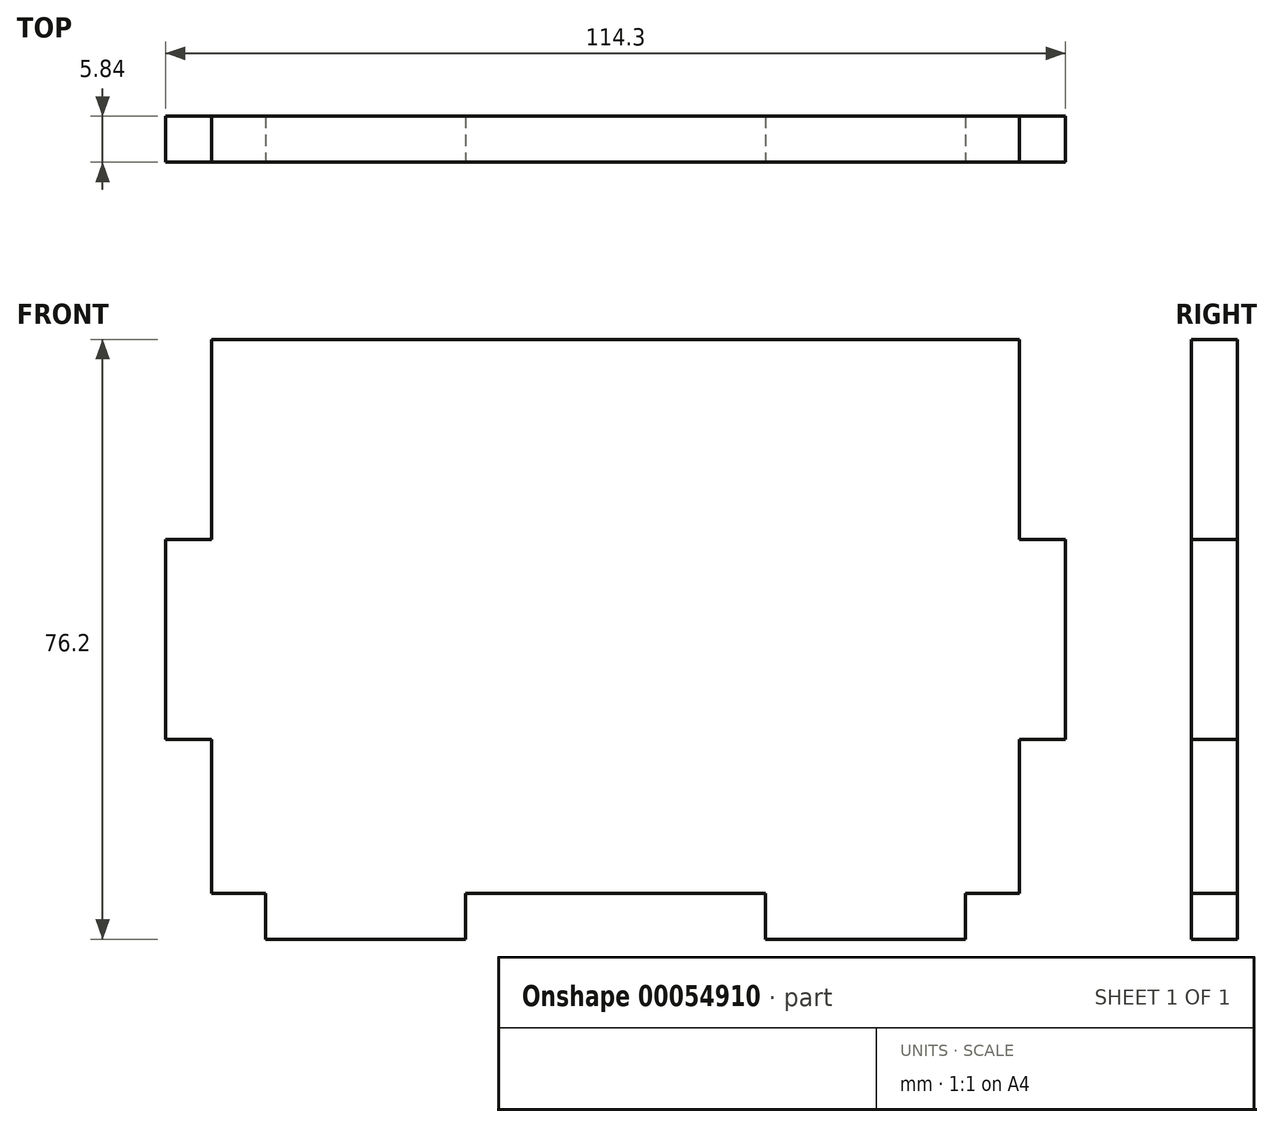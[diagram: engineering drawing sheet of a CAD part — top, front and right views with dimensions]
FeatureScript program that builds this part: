
annotation { "Feature Type Name" : "Feature", "Feature Type Description" : "" }
export const myFeature = defineFeature(function(context is Context, id is Id, definition is map)
    precondition{}
    {
        {
            var Q0;
            Q0=qCreatedBy(makeId("Front.planeOp"),FACE);
            var sketch = newSketch(context, id + "F0", { "sketchPlane" : qUnion([Q0])});
            skLineSegment(sketch, "E0.bottom", {"start": v(-48.17, 28.9) * mm, "end": v(66.13, 28.9) * mm});
            skLineSegment(sketch, "E0.top", {"start": v(-48.17, -47.3) * mm, "end": v(66.13, -47.3) * mm});
            skLineSegment(sketch, "E0.left", {"start": v(-48.17, 28.9) * mm, "end": v(-48.17, -47.3) * mm});
            skLineSegment(sketch, "E0.right", {"start": v(66.13, 28.9) * mm, "end": v(66.13, -47.3) * mm});
            skSolve(sketch);
        }
        {
            var Q0;
            Q0=makeQuery(id+"F0.imprint","IMPRINT",FACE,{"disambiguationData":[TD([[makeQuery(id+"F0.imprint","IMPRINT",EDGE,{"derivedFrom":sQuery(id+"F0.wireOp",EDGE,"E0.bottom")}),-1.0]])]});
            extrude(context, id + "F1", {"entities" : qUnion([Q0]), "depth" : 5.84 * mm});
        }
        {
            var Q0;
            Q0=makeQuery(id+"F1.opExtrude","CAP_FACE",FACE,{"disambiguationData":[OSD([sQuery(id+"F0.wireOp",EDGE,"E0.bottom"),sQuery(id+"F0.wireOp",EDGE,"E0.top"),sQuery(id+"F0.wireOp",EDGE,"E0.left"),sQuery(id+"F0.wireOp",EDGE,"E0.right")])],"isStart":false});
            var sketch = newSketch(context, id + "F2", { "sketchPlane" : qUnion([Q0])});
            skLineSegment(sketch, "E1.bottom", {"start": v(-35.47, -47.3) * mm, "end": v(-10.07, -47.3) * mm});
            skLineSegment(sketch, "E1.top", {"start": v(-35.47, -41.45) * mm, "end": v(-10.07, -41.45) * mm});
            skLineSegment(sketch, "E1.left", {"start": v(-35.47, -47.3) * mm, "end": v(-35.47, -41.45) * mm});
            skLineSegment(sketch, "E1.right", {"start": v(-10.07, -47.3) * mm, "end": v(-10.07, -41.45) * mm});
            skLineSegment(sketch, "E2.bottom", {"start": v(28.03, -47.3) * mm, "end": v(53.43, -47.3) * mm});
            skLineSegment(sketch, "E2.top", {"start": v(28.03, -41.45) * mm, "end": v(53.43, -41.45) * mm});
            skLineSegment(sketch, "E2.left", {"start": v(28.03, -47.3) * mm, "end": v(28.03, -41.45) * mm});
            skLineSegment(sketch, "E2.right", {"start": v(53.43, -47.3) * mm, "end": v(53.43, -41.45) * mm});
            skLineSegment(sketch, "E3.bottom", {"start": v(-48.17, -21.9) * mm, "end": v(-42.32, -21.9) * mm});
            skLineSegment(sketch, "E3.top", {"start": v(-48.17, 3.5) * mm, "end": v(-42.32, 3.5) * mm});
            skLineSegment(sketch, "E3.left", {"start": v(-48.17, -21.9) * mm, "end": v(-48.17, 3.5) * mm});
            skLineSegment(sketch, "E3.right", {"start": v(-42.32, -21.9) * mm, "end": v(-42.32, 3.5) * mm});
            skLineSegment(sketch, "E4.bottom", {"start": v(66.13, -21.9) * mm, "end": v(60.3, -21.9) * mm});
            skLineSegment(sketch, "E4.top", {"start": v(66.13, 3.5) * mm, "end": v(60.3, 3.5) * mm});
            skLineSegment(sketch, "E4.left", {"start": v(66.13, -21.9) * mm, "end": v(66.13, 3.5) * mm});
            skLineSegment(sketch, "E4.right", {"start": v(60.3, -21.9) * mm, "end": v(60.3, 3.5) * mm});
            skLineSegment(sketch, "E5", {"start": v(-42.32, 3.5) * mm, "end": v(-42.32, 28.9) * mm});
            skLineSegment(sketch, "E6", {"start": v(-42.32, -21.9) * mm, "end": v(-42.32, -41.45) * mm});
            skLineSegment(sketch, "E7", {"start": v(-35.47, -41.45) * mm, "end": v(-42.32, -41.45) * mm});
            skLineSegment(sketch, "E8", {"start": v(60.3, -21.9) * mm, "end": v(60.3, -41.45) * mm});
            skLineSegment(sketch, "E9", {"start": v(53.43, -41.45) * mm, "end": v(60.3, -41.45) * mm});
            skLineSegment(sketch, "E10", {"start": v(-10.07, -41.45) * mm, "end": v(28.03, -41.45) * mm});
            skLineSegment(sketch, "E11", {"start": v(60.3, 3.5) * mm, "end": v(60.3, 28.9) * mm});
            skLineSegment(sketch, "E12", {"start": v(60.3, 28.9) * mm, "end": v(-42.32, 28.9) * mm});
            skLineSegment(sketch, "E13.bottom", {"start": v(-16.42, 28.9) * mm, "end": v(34.38, 28.9) * mm});
            skLineSegment(sketch, "E13.top", {"start": v(-16.42, 26.37) * mm, "end": v(34.38, 26.37) * mm});
            skLineSegment(sketch, "E13.left", {"start": v(-16.42, 28.9) * mm, "end": v(-16.42, 26.37) * mm});
            skLineSegment(sketch, "E13.right", {"start": v(34.38, 28.9) * mm, "end": v(34.38, 26.37) * mm});
            skPoint(sketch, "E14", {"position": v(8.98, 26.37) * mm});
            skPoint(sketch, "E15", {"position": v(8.98, -47.3) * mm});
            skLineSegment(sketch, "E16.bottom", {"start": v(-29.62, 28.9) * mm, "end": v(-42.32, 28.9) * mm});
            skLineSegment(sketch, "E16.top", {"start": v(-29.62, 26.37) * mm, "end": v(-42.32, 26.37) * mm});
            skLineSegment(sketch, "E16.left", {"start": v(-29.62, 28.9) * mm, "end": v(-29.62, 26.37) * mm});
            skLineSegment(sketch, "E16.right", {"start": v(-42.32, 28.9) * mm, "end": v(-42.32, 26.37) * mm});
            skLineSegment(sketch, "E17.bottom", {"start": v(60.3, 28.9) * mm, "end": v(47.6, 28.9) * mm});
            skLineSegment(sketch, "E17.top", {"start": v(60.3, 26.37) * mm, "end": v(47.6, 26.37) * mm});
            skLineSegment(sketch, "E17.left", {"start": v(60.3, 28.9) * mm, "end": v(60.3, 26.37) * mm});
            skLineSegment(sketch, "E17.right", {"start": v(47.6, 28.9) * mm, "end": v(47.6, 26.37) * mm});
            skSolve(sketch);
        }
        {
            var Q0;
            {var subQ0=sQuery(id+"F2.wireOp",EDGE,"E3.top");Q0=makeQuery(id+"F2.imprint","IMPRINT",FACE,{"disambiguationData":[TD([[makeQuery(id+"F2.imprint","IMPRINT",EDGE,{"derivedFrom":subQ0}),1.0]])]});}
            var Q1;
            {var subQ1=sQuery(id+"F2.wireOp",EDGE,"E1.left");Q1=makeQuery(id+"F2.imprint","IMPRINT",FACE,{"disambiguationData":[TD([[makeQuery(id+"F2.imprint","IMPRINT",EDGE,{"derivedFrom":subQ1}),1.0]])]});}
            var Q2;
            {var subQ0=sQuery(id+"F2.wireOp",EDGE,"E1.right");Q2=makeQuery(id+"F2.imprint","IMPRINT",FACE,{"disambiguationData":[TD([[makeQuery(id+"F2.imprint","IMPRINT",EDGE,{"derivedFrom":subQ0}),-1.0]])]});}
            var Q3;
            {var subQ4=sQuery(id+"F2.wireOp",EDGE,"E2.right");Q3=makeQuery(id+"F2.imprint","IMPRINT",FACE,{"disambiguationData":[TD([[makeQuery(id+"F2.imprint","IMPRINT",EDGE,{"derivedFrom":subQ4}),-1.0]])]});}
            var Q4;
            {var subQ0=sQuery(id+"F2.wireOp",EDGE,"E4.top");Q4=makeQuery(id+"F2.imprint","IMPRINT",FACE,{"disambiguationData":[TD([[makeQuery(id+"F2.imprint","IMPRINT",EDGE,{"derivedFrom":subQ0}),-1.0]])]});}
            var Q5;
            Q5=makeQuery(id+"F2.imprint","IMPRINT",FACE,{"disambiguationData":[TD([[makeQuery(id+"F2.imprint","IMPRINT",EDGE,{"derivedFrom":sQuery(id+"F2.wireOp",EDGE,"E13.bottom")}),-1.0]])]});
            var Q6;
            Q6=makeQuery(id+"F2.imprint","IMPRINT",FACE,{"disambiguationData":[TD([[makeQuery(id+"F2.imprint","IMPRINT",EDGE,{"derivedFrom":sQuery(id+"F2.wireOp",EDGE,"E16.bottom")}),-1.0]])]});
            var Q7;
            Q7=makeQuery(id+"F2.imprint","IMPRINT",FACE,{"disambiguationData":[TD([[makeQuery(id+"F2.imprint","IMPRINT",EDGE,{"derivedFrom":sQuery(id+"F2.wireOp",EDGE,"E17.bottom")}),-1.0]])]});
            var Q8;
            Q8=makeQuery(id+"F1.opExtrude","CAP_FACE",FACE,{"disambiguationData":[OSD([sQuery(id+"F0.wireOp",EDGE,"E0.bottom"),sQuery(id+"F0.wireOp",EDGE,"E0.top"),sQuery(id+"F0.wireOp",EDGE,"E0.left"),sQuery(id+"F0.wireOp",EDGE,"E0.right")])],"isStart":true});
            extrude(context, id + "F3", {"entities" : qUnion([Q0, Q1, Q2, Q3, Q4, Q5, Q6, Q7]), "operationType" : NewBodyOperationType.REMOVE, "endBound" : BoundingType.UP_TO_SURFACE, "oppositeDirection" : true, "endBoundEntityFace" : qUnion([Q8]), "depth" : 25.4 * mm});
        }
    });
